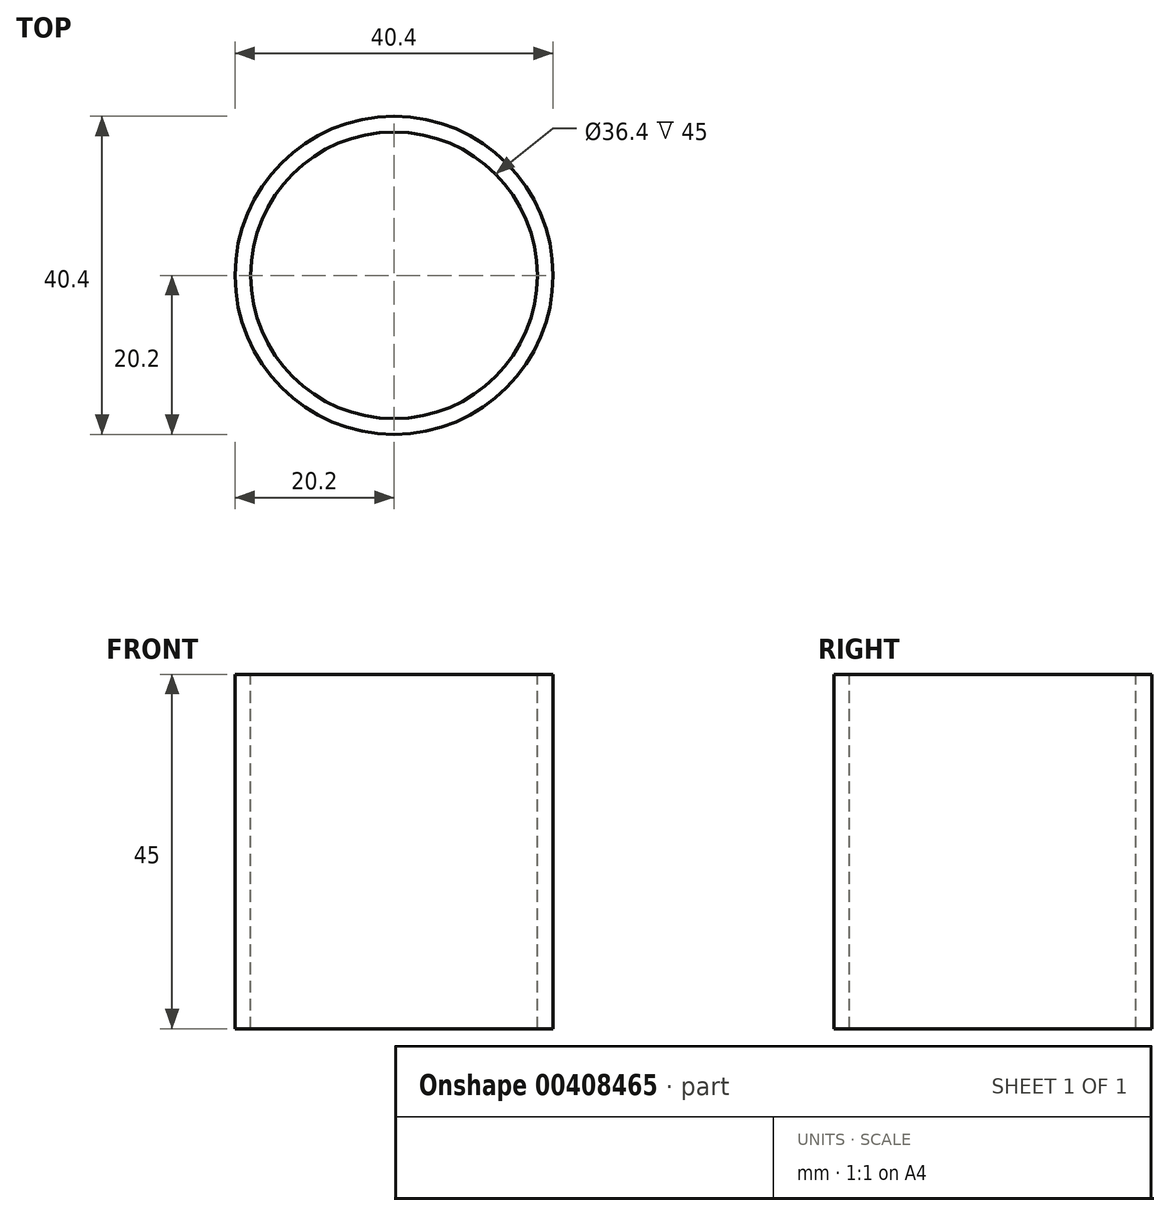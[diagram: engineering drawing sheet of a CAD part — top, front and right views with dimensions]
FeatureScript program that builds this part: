
annotation { "Feature Type Name" : "Feature", "Feature Type Description" : "" }
export const myFeature = defineFeature(function(context is Context, id is Id, definition is map)
    precondition{}
    {
        {
            var Q0;
            Q0=qCreatedBy(makeId("Front.planeOp"),FACE);
            var sketch = newSketch(context, id + "F0", { "sketchPlane" : qUnion([Q0])});
            skLineSegment(sketch, "E0", {"start": v(-18.2, 20) * mm, "end": v(-18.2, -25) * mm});
            skLineSegment(sketch, "E1.0", {"start": v(-20.2, 20) * mm, "end": v(-20.2, -25) * mm});
            skLineSegment(sketch, "E2", {"start": v(-20.2, 20) * mm, "end": v(-18.2, 20) * mm});
            skLineSegment(sketch, "E3", {"start": v(-20.2, -25) * mm, "end": v(-18.2, -25) * mm});
            skSolve(sketch);
        }
        {
            var Q0;
            Q0=qCreatedBy(makeId("Front.planeOp"),FACE);
            var sketch = newSketch(context, id + "F1", { "sketchPlane" : qUnion([Q0])});
            skLineSegment(sketch, "E4", {"start": v(0, 34.34) * mm, "end": v(0, -45.56) * mm, "construction": true});
            skSolve(sketch);
        }
        {
            var Q0;
            Q0=makeQuery(id+"F0.imprint","IMPRINT",FACE,{"disambiguationData":[TD([[makeQuery(id+"F0.imprint","IMPRINT",EDGE,{"derivedFrom":sQuery(id+"F0.wireOp",EDGE,"E0")}),-1.0]])]});
            var Q1;
            Q1=sQuery(id+"F1.wireOp",EDGE,"E4");
            revolve(context, id + "F2", {"entities" : qUnion([Q0]), "axis" : qUnion([Q1]), "revolveType" : RevolveType.FULL});
        }
    });
